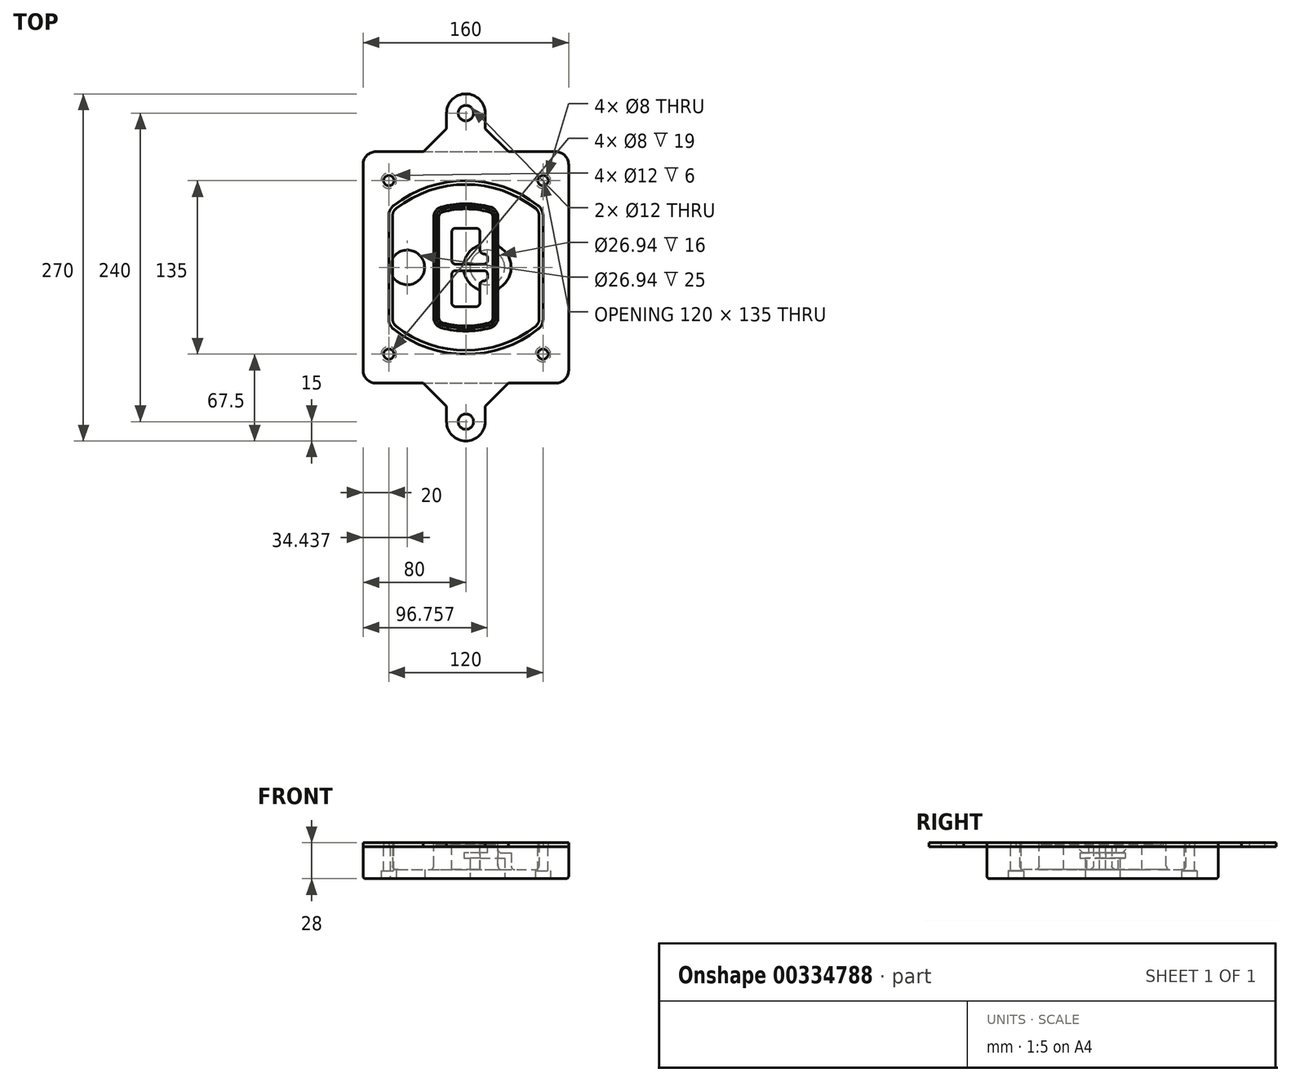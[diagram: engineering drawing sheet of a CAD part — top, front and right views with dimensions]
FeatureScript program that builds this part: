
annotation { "Feature Type Name" : "Feature", "Feature Type Description" : "" }
export const myFeature = defineFeature(function(context is Context, id is Id, definition is map)
    precondition{}
    {
        {
            var Q0;
            Q0=qCreatedBy(makeId("Top.planeOp"),FACE);
            var sketch = newSketch(context, id + "F0", { "sketchPlane" : qUnion([Q0])});
            skPoint(sketch, "E0.rect.middle", {"position": v(0, 0) * mm});
            skLineSegment(sketch, "E1.bottom", {"start": v(-70, -90) * mm, "end": v(70, -90) * mm});
            skLineSegment(sketch, "E1.top", {"start": v(-70, 90) * mm, "end": v(70, 90) * mm});
            skLineSegment(sketch, "E1.left", {"start": v(-80, -80) * mm, "end": v(-80, 80) * mm});
            skLineSegment(sketch, "E1.right", {"start": v(80, -80) * mm, "end": v(80, 80) * mm});
            skLineSegment(sketch, "E2", {"start": v(-80, 90) * mm, "end": v(80, -90) * mm, "construction": true});
            skLineSegment(sketch, "E3", {"start": v(80, 90) * mm, "end": v(-80, -90) * mm, "construction": true});
            skCircle(sketch, "E4", {"center": v(-60, 67.5) * mm, "radius": 4 * mm});
            skCircle(sketch, "E5", {"center": v(60, 67.5) * mm, "radius": 4 * mm});
            skCircle(sketch, "E6", {"center": v(60, -67.5) * mm, "radius": 4 * mm});
            skCircle(sketch, "E7", {"center": v(-60, -67.5) * mm, "radius": 4 * mm});
            skLineSegment(sketch, "E8", {"start": v(-60, 67.5) * mm, "end": v(60, 67.5) * mm, "construction": true});
            skLineSegment(sketch, "E9", {"start": v(60, 67.5) * mm, "end": v(60, -67.5) * mm, "construction": true});
            skLineSegment(sketch, "E10", {"start": v(60, -67.5) * mm, "end": v(-60, -67.5) * mm, "construction": true});
            skLineSegment(sketch, "E11", {"start": v(-60, -67.5) * mm, "end": v(-60, 67.5) * mm, "construction": true});
            skLineSegment(sketch, "E12", {"start": v(-60, 40.3) * mm, "end": v(-60, -40.3) * mm});
            skLineSegment(sketch, "E13", {"start": v(60, 40.3) * mm, "end": v(60, -40.3) * mm});
            skArc(sketch, "E14", {"start": v(56.15, 48.18) * mm, "mid": v(0, 67.5) * mm, "end": v(-56.15, 48.18) * mm});
            skArc(sketch, "E15", {"start": v(-56.15, -48.18) * mm, "mid": v(0, -67.5) * mm, "end": v(56.15, -48.18) * mm});
            skLineSegment(sketch, "E16", {"start": v(-60, 0) * mm, "end": v(60, 0) * mm, "construction": true});
            skPoint(sketch, "E17.visualSharp", {"position": v(-60, -45) * mm});
            skArc(sketch, "E17.filletArc", {"start": v(-60, -40.3) * mm, "mid": v(-58.99, -44.68) * mm, "end": v(-56.15, -48.18) * mm});
            skPoint(sketch, "E18.visualSharp", {"position": v(-60, 45) * mm});
            skArc(sketch, "E18.filletArc", {"start": v(-56.15, 48.18) * mm, "mid": v(-58.99, 44.68) * mm, "end": v(-60, 40.3) * mm});
            skPoint(sketch, "E19.visualSharp", {"position": v(60, 45) * mm});
            skArc(sketch, "E19.filletArc", {"start": v(60, 40.3) * mm, "mid": v(58.99, 44.68) * mm, "end": v(56.15, 48.18) * mm});
            skPoint(sketch, "E20.visualSharp", {"position": v(60, -45) * mm});
            skArc(sketch, "E20.filletArc", {"start": v(56.15, -48.18) * mm, "mid": v(58.99, -44.68) * mm, "end": v(60, -40.3) * mm});
            skPoint(sketch, "E21.visualSharp", {"position": v(-80, 90) * mm});
            skArc(sketch, "E21.filletArc", {"start": v(-70, 90) * mm, "mid": v(-77.07, 87.07) * mm, "end": v(-80, 80) * mm});
            skPoint(sketch, "E22.visualSharp", {"position": v(80, 90) * mm});
            skArc(sketch, "E22.filletArc", {"start": v(80, 80) * mm, "mid": v(77.07, 87.07) * mm, "end": v(70, 90) * mm});
            skPoint(sketch, "E23.visualSharp", {"position": v(80, -90) * mm});
            skArc(sketch, "E23.filletArc", {"start": v(70, -90) * mm, "mid": v(77.07, -87.07) * mm, "end": v(80, -80) * mm});
            skPoint(sketch, "E24.visualSharp", {"position": v(-80, -90) * mm});
            skArc(sketch, "E24.filletArc", {"start": v(-80, -80) * mm, "mid": v(-77.07, -87.07) * mm, "end": v(-70, -90) * mm});
            skArc(sketch, "E25.0", {"start": v(57, 40.3) * mm, "mid": v(56.3, 43.36) * mm, "end": v(54.3, 45.81) * mm});
            skLineSegment(sketch, "E25.1", {"start": v(57, 40.3) * mm, "end": v(57, -40.3) * mm});
            skArc(sketch, "E25.2", {"start": v(54.3, -45.81) * mm, "mid": v(56.3, -43.36) * mm, "end": v(57, -40.3) * mm});
            skArc(sketch, "E25.3", {"start": v(-54.3, -45.81) * mm, "mid": v(0, -64.5) * mm, "end": v(54.3, -45.81) * mm});
            skArc(sketch, "E25.4", {"start": v(-57, -40.3) * mm, "mid": v(-56.3, -43.36) * mm, "end": v(-54.3, -45.81) * mm});
            skArc(sketch, "E25.5", {"start": v(54.3, 45.81) * mm, "mid": v(0, 64.5) * mm, "end": v(-54.3, 45.81) * mm});
            skLineSegment(sketch, "E25.6", {"start": v(-57, 40.3) * mm, "end": v(-57, -40.3) * mm});
            skArc(sketch, "E25.7", {"start": v(-54.3, 45.81) * mm, "mid": v(-56.3, 43.36) * mm, "end": v(-57, 40.3) * mm});
            skArc(sketch, "E26.0", {"start": v(-58.62, 51.33) * mm, "mid": v(-62.58, 46.43) * mm, "end": v(-64, 40.3) * mm});
            skArc(sketch, "E26.1", {"start": v(58.62, 51.33) * mm, "mid": v(0, 71.5) * mm, "end": v(-58.62, 51.33) * mm});
            skArc(sketch, "E26.2", {"start": v(64, 40.3) * mm, "mid": v(62.58, 46.43) * mm, "end": v(58.62, 51.33) * mm});
            skLineSegment(sketch, "E26.3", {"start": v(64, 40.3) * mm, "end": v(64, -40.3) * mm});
            skArc(sketch, "E26.4", {"start": v(58.62, -51.33) * mm, "mid": v(62.58, -46.43) * mm, "end": v(64, -40.3) * mm});
            skLineSegment(sketch, "E26.5", {"start": v(-64, 40.3) * mm, "end": v(-64, -40.3) * mm});
            skArc(sketch, "E26.6", {"start": v(-58.62, -51.33) * mm, "mid": v(0, -71.5) * mm, "end": v(58.62, -51.33) * mm});
            skArc(sketch, "E26.7", {"start": v(-64, -40.3) * mm, "mid": v(-62.58, -46.43) * mm, "end": v(-58.62, -51.33) * mm});
            skSolve(sketch);
        }
        {
            var Q0;
            Q0=makeQuery(id+"F0.imprint","IMPRINT",FACE,{"disambiguationData":[TD([[makeQuery(id+"F0.imprint","IMPRINT",EDGE,{"derivedFrom":sQuery(id+"F0.wireOp",EDGE,"E1.bottom")}),1.0]])]});
            var Q1;
            Q1=makeQuery(id+"F0.imprint","IMPRINT",FACE,{"disambiguationData":[TD([[makeQuery(id+"F0.imprint","IMPRINT",EDGE,{"derivedFrom":sQuery(id+"F0.wireOp",EDGE,"E12")}),1.0]])]});
            var Q2;
            Q2=makeQuery(id+"F0.imprint","IMPRINT",FACE,{"disambiguationData":[TD([[makeQuery(id+"F0.imprint","IMPRINT",EDGE,{"derivedFrom":sQuery(id+"F0.wireOp",EDGE,"E25.0")}),1.0]])]});
            var Q3;
            Q3=makeQuery(id+"F0.imprint","IMPRINT",FACE,{"disambiguationData":[TD([[makeQuery(id+"F0.imprint","IMPRINT",EDGE,{"derivedFrom":sQuery(id+"F0.wireOp",EDGE,"E12")}),-1.0]])]});
            extrude(context, id + "F1", {"entities" : qUnion([Q0, Q1, Q2, Q3]), "oppositeDirection" : true, "depth" : 25 * mm});
        }
        {
            var Q0;
            Q0=makeQuery(id+"F0.imprint","IMPRINT",FACE,{"disambiguationData":[TD([[makeQuery(id+"F0.imprint","IMPRINT",EDGE,{"derivedFrom":sQuery(id+"F0.wireOp",EDGE,"E12")}),1.0]])]});
            extrude(context, id + "F2", {"entities" : qUnion([Q0]), "operationType" : NewBodyOperationType.ADD, "depth" : 3 * mm});
        }
        {
            var Q0;
            Q0=makeQuery(id+"F0.imprint","IMPRINT",FACE,{"disambiguationData":[TD([[makeQuery(id+"F0.imprint","IMPRINT",EDGE,{"derivedFrom":sQuery(id+"F0.wireOp",EDGE,"E25.0")}),1.0]])]});
            extrude(context, id + "F3", {"entities" : qUnion([Q0]), "operationType" : NewBodyOperationType.REMOVE, "oppositeDirection" : true, "depth" : 18 * mm, "offsetDistance" : 25 * mm});
        }
        {
            var Q0;
            Q0=makeQuery(id+"F2.opExtrude","CAP_FACE",FACE,{"disambiguationData":[OSD([sQuery(id+"F0.wireOp",EDGE,"E12"),sQuery(id+"F0.wireOp",EDGE,"E13"),sQuery(id+"F0.wireOp",EDGE,"E14"),sQuery(id+"F0.wireOp",EDGE,"E15"),sQuery(id+"F0.wireOp",EDGE,"E17.filletArc"),sQuery(id+"F0.wireOp",EDGE,"E18.filletArc"),sQuery(id+"F0.wireOp",EDGE,"E19.filletArc"),sQuery(id+"F0.wireOp",EDGE,"E20.filletArc"),sQuery(id+"F0.wireOp",EDGE,"E25.0"),sQuery(id+"F0.wireOp",EDGE,"E25.1"),sQuery(id+"F0.wireOp",EDGE,"E25.2"),sQuery(id+"F0.wireOp",EDGE,"E25.3"),sQuery(id+"F0.wireOp",EDGE,"E25.4"),sQuery(id+"F0.wireOp",EDGE,"E25.5"),sQuery(id+"F0.wireOp",EDGE,"E25.6"),sQuery(id+"F0.wireOp",EDGE,"E25.7")])],"isStart":false});
            var sketch = newSketch(context, id + "F4", { "sketchPlane" : qUnion([Q0])});
            skArc(sketch, "E27.0", {"start": v(-19.08, -46.97) * mm, "mid": v(0, -49.5) * mm, "end": v(19.08, -46.97) * mm});
            skArc(sketch, "E28.0", {"start": v(19.08, 46.97) * mm, "mid": v(0, 49.5) * mm, "end": v(-19.08, 46.97) * mm});
            skLineSegment(sketch, "E29", {"start": v(-25, 39.25) * mm, "end": v(-25, -39.25) * mm});
            skLineSegment(sketch, "E30", {"start": v(25, 39.25) * mm, "end": v(25, -39.25) * mm});
            skLineSegment(sketch, "E31", {"start": v(-25, 45.1) * mm, "end": v(25, 45.1) * mm, "construction": true});
            skLineSegment(sketch, "E32", {"start": v(-25, -45.1) * mm, "end": v(25, -45.1) * mm, "construction": true});
            skPoint(sketch, "E33.visualSharp", {"position": v(-25, 45.1) * mm});
            skArc(sketch, "E33.filletArc", {"start": v(-19.08, 46.97) * mm, "mid": v(-23.35, 44.11) * mm, "end": v(-25, 39.25) * mm});
            skPoint(sketch, "E34.visualSharp", {"position": v(25, 45.1) * mm});
            skArc(sketch, "E34.filletArc", {"start": v(25, 39.25) * mm, "mid": v(23.35, 44.11) * mm, "end": v(19.08, 46.97) * mm});
            skPoint(sketch, "E35.visualSharp", {"position": v(25, -45.1) * mm});
            skArc(sketch, "E35.filletArc", {"start": v(19.08, -46.97) * mm, "mid": v(23.35, -44.11) * mm, "end": v(25, -39.25) * mm});
            skPoint(sketch, "E36.visualSharp", {"position": v(-25, -45.1) * mm});
            skArc(sketch, "E36.filletArc", {"start": v(-25, -39.25) * mm, "mid": v(-23.35, -44.11) * mm, "end": v(-19.08, -46.97) * mm});
            skArc(sketch, "E37.0", {"start": v(54.3, 45.81) * mm, "mid": v(0, 64.5) * mm, "end": v(-54.3, 45.81) * mm});
            skArc(sketch, "E37.1", {"start": v(-54.3, 45.81) * mm, "mid": v(-56.3, 43.36) * mm, "end": v(-57, 40.3) * mm});
            skLineSegment(sketch, "E37.2", {"start": v(-57, 40.3) * mm, "end": v(-57, -40.3) * mm});
            skArc(sketch, "E37.3", {"start": v(-57, -40.3) * mm, "mid": v(-56.3, -43.36) * mm, "end": v(-54.3, -45.81) * mm});
            skArc(sketch, "E37.4", {"start": v(-54.3, -45.81) * mm, "mid": v(0, -64.5) * mm, "end": v(54.3, -45.81) * mm});
            skArc(sketch, "E37.5", {"start": v(54.3, -45.81) * mm, "mid": v(56.3, -43.36) * mm, "end": v(57, -40.3) * mm});
            skLineSegment(sketch, "E37.6", {"start": v(57, 40.3) * mm, "end": v(57, -40.3) * mm});
            skArc(sketch, "E37.7", {"start": v(57, 40.3) * mm, "mid": v(56.3, 43.36) * mm, "end": v(54.3, 45.81) * mm});
            skLineSegment(sketch, "E38.0", {"start": v(23, 39.25) * mm, "end": v(23, -39.25) * mm});
            skArc(sketch, "E38.1", {"start": v(18.56, -45.04) * mm, "mid": v(21.76, -42.9) * mm, "end": v(23, -39.25) * mm});
            skArc(sketch, "E38.2", {"start": v(-18.56, -45.04) * mm, "mid": v(0, -47.5) * mm, "end": v(18.56, -45.04) * mm});
            skArc(sketch, "E38.3", {"start": v(-23, -39.25) * mm, "mid": v(-21.76, -42.9) * mm, "end": v(-18.56, -45.04) * mm});
            skLineSegment(sketch, "E38.4", {"start": v(-23, 39.25) * mm, "end": v(-23, -39.25) * mm});
            skArc(sketch, "E38.5", {"start": v(23, 39.25) * mm, "mid": v(21.76, 42.9) * mm, "end": v(18.56, 45.04) * mm});
            skArc(sketch, "E38.6", {"start": v(-18.56, 45.04) * mm, "mid": v(-21.76, 42.9) * mm, "end": v(-23, 39.25) * mm});
            skArc(sketch, "E38.7", {"start": v(18.56, 45.04) * mm, "mid": v(0, 47.5) * mm, "end": v(-18.56, 45.04) * mm});
            skArc(sketch, "E39.0", {"start": v(21, 39.25) * mm, "mid": v(20.18, 41.68) * mm, "end": v(18.04, 43.1) * mm});
            skLineSegment(sketch, "E39.1", {"start": v(21, 39.25) * mm, "end": v(21, -39.25) * mm});
            skArc(sketch, "E39.2", {"start": v(18.04, -43.1) * mm, "mid": v(20.18, -41.68) * mm, "end": v(21, -39.25) * mm});
            skArc(sketch, "E39.3", {"start": v(-18.04, -43.1) * mm, "mid": v(0, -45.5) * mm, "end": v(18.04, -43.1) * mm});
            skArc(sketch, "E39.4", {"start": v(-21, -39.25) * mm, "mid": v(-20.18, -41.68) * mm, "end": v(-18.04, -43.1) * mm});
            skArc(sketch, "E39.5", {"start": v(18.04, 43.1) * mm, "mid": v(0, 45.5) * mm, "end": v(-18.04, 43.1) * mm});
            skLineSegment(sketch, "E39.6", {"start": v(-21, 39.25) * mm, "end": v(-21, -39.25) * mm});
            skArc(sketch, "E39.7", {"start": v(-18.04, 43.1) * mm, "mid": v(-20.18, 41.68) * mm, "end": v(-21, 39.25) * mm});
            skLineSegment(sketch, "E40", {"start": v(-25, 0) * mm, "end": v(25, 0) * mm, "construction": true});
            skLineSegment(sketch, "E41", {"start": v(-11, 5.5) * mm, "end": v(-11, 27.5) * mm});
            skLineSegment(sketch, "E42", {"start": v(-8, 30.5) * mm, "end": v(8, 30.5) * mm});
            skLineSegment(sketch, "E43", {"start": v(11, 27.5) * mm, "end": v(11, 13.5) * mm});
            skLineSegment(sketch, "E44", {"start": v(14, 10.5) * mm, "end": v(14, 10.5) * mm});
            skLineSegment(sketch, "E45", {"start": v(17, 7.5) * mm, "end": v(17, 5.5) * mm});
            skLineSegment(sketch, "E46", {"start": v(14, 2.5) * mm, "end": v(-8, 2.5) * mm});
            skPoint(sketch, "E47.visualSharp", {"position": v(-11, 30.5) * mm});
            skArc(sketch, "E47.filletArc", {"start": v(-8, 30.5) * mm, "mid": v(-10.12, 29.62) * mm, "end": v(-11, 27.5) * mm});
            skPoint(sketch, "E48.visualSharp", {"position": v(11, 30.5) * mm});
            skArc(sketch, "E48.filletArc", {"start": v(11, 27.5) * mm, "mid": v(10.12, 29.62) * mm, "end": v(8, 30.5) * mm});
            skPoint(sketch, "E49.visualSharp", {"position": v(11, 10.5) * mm});
            skArc(sketch, "E49.filletArc", {"start": v(11, 13.5) * mm, "mid": v(11.88, 11.38) * mm, "end": v(14, 10.5) * mm});
            skPoint(sketch, "E50.visualSharp", {"position": v(17, 10.5) * mm});
            skArc(sketch, "E50.filletArc", {"start": v(17, 7.5) * mm, "mid": v(16.12, 9.62) * mm, "end": v(14, 10.5) * mm});
            skPoint(sketch, "E51.visualSharp", {"position": v(17, 2.5) * mm});
            skArc(sketch, "E51.filletArc", {"start": v(14, 2.5) * mm, "mid": v(16.12, 3.38) * mm, "end": v(17, 5.5) * mm});
            skPoint(sketch, "E52.visualSharp", {"position": v(-11, 2.5) * mm});
            skArc(sketch, "E52.filletArc", {"start": v(-11, 5.5) * mm, "mid": v(-10.12, 3.38) * mm, "end": v(-8, 2.5) * mm});
            skLineSegment(sketch, "E53.0.MirrorCS", {"start": v(14, -2.5) * mm, "end": v(-8, -2.5) * mm});
            skArc(sketch, "E54.0.MirrorCS", {"start": v(-11, -5.5) * mm, "mid": v(-10.12, -3.38) * mm, "end": v(-8, -2.5) * mm});
            skLineSegment(sketch, "E55.0.MirrorCS", {"start": v(-11, -5.5) * mm, "end": v(-11, -27.5) * mm});
            skArc(sketch, "E56.0.MirrorCS", {"start": v(-8, -30.5) * mm, "mid": v(-10.12, -29.62) * mm, "end": v(-11, -27.5) * mm});
            skLineSegment(sketch, "E57.0.MirrorCS", {"start": v(-8, -30.5) * mm, "end": v(8, -30.5) * mm});
            skArc(sketch, "E58.0.MirrorCS", {"start": v(11, -27.5) * mm, "mid": v(10.12, -29.62) * mm, "end": v(8, -30.5) * mm});
            skLineSegment(sketch, "E59.0.MirrorCS", {"start": v(11, -27.5) * mm, "end": v(11, -13.5) * mm});
            skArc(sketch, "E60.0.MirrorCS", {"start": v(11, -13.5) * mm, "mid": v(11.88, -11.38) * mm, "end": v(14, -10.5) * mm});
            skArc(sketch, "E61.0.MirrorCS", {"start": v(17, -7.5) * mm, "mid": v(16.12, -9.62) * mm, "end": v(14, -10.5) * mm});
            skLineSegment(sketch, "E62.0.MirrorCS", {"start": v(17, -7.5) * mm, "end": v(17, -5.5) * mm});
            skArc(sketch, "E63.0.MirrorCS", {"start": v(14, -2.5) * mm, "mid": v(16.12, -3.38) * mm, "end": v(17, -5.5) * mm});
            skSolve(sketch);
        }
        {
            var Q0;
            Q0=makeQuery(id+"F4.imprint","IMPRINT",FACE,{"disambiguationData":[TD([[makeQuery(id+"F4.imprint","IMPRINT",EDGE,{"derivedFrom":sQuery(id+"F4.wireOp",EDGE,"E27.0")}),1.0]])]});
            var Q1;
            Q1=makeQuery(id+"F4.imprint","IMPRINT",FACE,{"disambiguationData":[TD([[makeQuery(id+"F4.imprint","IMPRINT",EDGE,{"derivedFrom":sQuery(id+"F4.wireOp",EDGE,"E38.0")}),-1.0]])]});
            var Q2;
            Q2=makeQuery(id+"F4.imprint","IMPRINT",FACE,{"disambiguationData":[TD([[makeQuery(id+"F4.imprint","IMPRINT",EDGE,{"derivedFrom":sQuery(id+"F4.wireOp",EDGE,"E39.0")}),1.0]])]});
            extrude(context, id + "F5", {"entities" : qUnion([Q0, Q1, Q2]), "operationType" : NewBodyOperationType.ADD, "endBound" : BoundingType.UP_TO_NEXT, "oppositeDirection" : true, "depth" : 25 * mm});
        }
        {
            var Q0;
            Q0=makeQuery(id+"F4.imprint","IMPRINT",FACE,{"disambiguationData":[TD([[makeQuery(id+"F4.imprint","IMPRINT",EDGE,{"derivedFrom":sQuery(id+"F4.wireOp",EDGE,"E38.0")}),-1.0]])]});
            extrude(context, id + "F6", {"entities" : qUnion([Q0]), "operationType" : NewBodyOperationType.REMOVE, "oppositeDirection" : true, "depth" : 2 * mm});
        }
        {
            var Q0;
            Q0=makeQuery(id+"F1.opExtrude","CAP_FACE",FACE,{"disambiguationData":[OSD([sQuery(id+"F0.wireOp",EDGE,"E1.bottom"),sQuery(id+"F0.wireOp",EDGE,"E1.top"),sQuery(id+"F0.wireOp",EDGE,"E1.left"),sQuery(id+"F0.wireOp",EDGE,"E1.right"),sQuery(id+"F0.wireOp",EDGE,"E4"),sQuery(id+"F0.wireOp",EDGE,"E5"),sQuery(id+"F0.wireOp",EDGE,"E6"),sQuery(id+"F0.wireOp",EDGE,"E7"),sQuery(id+"F0.wireOp",EDGE,"E21.filletArc"),sQuery(id+"F0.wireOp",EDGE,"E22.filletArc"),sQuery(id+"F0.wireOp",EDGE,"E23.filletArc"),sQuery(id+"F0.wireOp",EDGE,"E24.filletArc")])],"isStart":false});
            var sketch = newSketch(context, id + "F7", { "sketchPlane" : qUnion([Q0])});
            skCircle(sketch, "E64", {"center": v(16.76, 0) * mm, "radius": 13.47 * mm});
            skCircle(sketch, "E65", {"center": v(-45.56, 0) * mm, "radius": 13.47 * mm});
            skLineSegment(sketch, "E66", {"start": v(80, 0) * mm, "end": v(-80, 0) * mm});
            skCircle(sketch, "E67", {"center": v(16.76, 0) * mm, "radius": 18.47 * mm});
            skCircle(sketch, "E68", {"center": v(60, -67.5) * mm, "radius": 6 * mm});
            skCircle(sketch, "E69", {"center": v(-60, -67.5) * mm, "radius": 6 * mm});
            skCircle(sketch, "E70", {"center": v(-60, 67.5) * mm, "radius": 6 * mm});
            skCircle(sketch, "E71", {"center": v(60, 67.5) * mm, "radius": 6 * mm});
            skSolve(sketch);
        }
        {
            var Q0;
            {var subQ1=sQuery(id+"F7.wireOp",EDGE,"E66");var subQ4=sQuery(id+"F7.wireOp",EDGE,"E64");var subQ6=makeQuery(id+"F7.imprint","INTERSECT",VERTEX,{"disambiguationData":[OD(0.0)],"derivedFrom":[subQ4,subQ1]});Q0=makeQuery(id+"F7.imprint","IMPRINT",FACE,{"disambiguationData":[TD([[makeQuery(id+"F7.imprint","IMPRINT",EDGE,{"disambiguationData":[TD([[subQ6,-1.0]])],"derivedFrom":subQ4}),-1.0]])]});}
            var Q1;
            {var subQ0=sQuery(id+"F7.wireOp",EDGE,"E66");var subQ1=sQuery(id+"F7.wireOp",EDGE,"E64");var subQ3=makeQuery(id+"F7.imprint","INTERSECT",VERTEX,{"disambiguationData":[OD(0.0)],"derivedFrom":[subQ1,subQ0]});Q1=makeQuery(id+"F7.imprint","IMPRINT",FACE,{"disambiguationData":[TD([[makeQuery(id+"F7.imprint","IMPRINT",EDGE,{"disambiguationData":[TD([[subQ3,-1.0]])],"derivedFrom":subQ1}),1.0]])]});}
            var Q2;
            {var subQ0=sQuery(id+"F7.wireOp",EDGE,"E66");var subQ1=sQuery(id+"F7.wireOp",EDGE,"E64");var subQ3=makeQuery(id+"F7.imprint","INTERSECT",VERTEX,{"disambiguationData":[OD(0.0)],"derivedFrom":[subQ1,subQ0]});Q2=makeQuery(id+"F7.imprint","IMPRINT",FACE,{"disambiguationData":[TD([[makeQuery(id+"F7.imprint","IMPRINT",EDGE,{"disambiguationData":[TD([[subQ3,1.0]])],"derivedFrom":subQ1}),1.0]])]});}
            var Q3;
            {var subQ1=sQuery(id+"F7.wireOp",EDGE,"E66");var subQ4=sQuery(id+"F7.wireOp",EDGE,"E64");var subQ6=makeQuery(id+"F7.imprint","INTERSECT",VERTEX,{"disambiguationData":[OD(0.0)],"derivedFrom":[subQ4,subQ1]});Q3=makeQuery(id+"F7.imprint","IMPRINT",FACE,{"disambiguationData":[TD([[makeQuery(id+"F7.imprint","IMPRINT",EDGE,{"disambiguationData":[TD([[subQ6,1.0]])],"derivedFrom":subQ4}),-1.0]])]});}
            extrude(context, id + "F8", {"entities" : qUnion([Q0, Q1, Q2, Q3]), "operationType" : NewBodyOperationType.ADD, "oppositeDirection" : true, "depth" : 20 * mm});
        }
        {
            var Q0;
            {var subQ0=sQuery(id+"F7.wireOp",EDGE,"E66");var subQ1=sQuery(id+"F7.wireOp",EDGE,"E64");var subQ3=makeQuery(id+"F7.imprint","INTERSECT",VERTEX,{"disambiguationData":[OD(0.0)],"derivedFrom":[subQ1,subQ0]});Q0=makeQuery(id+"F7.imprint","IMPRINT",FACE,{"disambiguationData":[TD([[makeQuery(id+"F7.imprint","IMPRINT",EDGE,{"disambiguationData":[TD([[subQ3,-1.0]])],"derivedFrom":subQ1}),1.0]])]});}
            var Q1;
            {var subQ0=sQuery(id+"F7.wireOp",EDGE,"E66");var subQ1=sQuery(id+"F7.wireOp",EDGE,"E64");var subQ3=makeQuery(id+"F7.imprint","INTERSECT",VERTEX,{"disambiguationData":[OD(0.0)],"derivedFrom":[subQ1,subQ0]});Q1=makeQuery(id+"F7.imprint","IMPRINT",FACE,{"disambiguationData":[TD([[makeQuery(id+"F7.imprint","IMPRINT",EDGE,{"disambiguationData":[TD([[subQ3,1.0]])],"derivedFrom":subQ1}),1.0]])]});}
            extrude(context, id + "F9", {"entities" : qUnion([Q0, Q1]), "operationType" : NewBodyOperationType.REMOVE, "oppositeDirection" : true, "depth" : 16 * mm});
        }
        {
            var Q0;
            {var subQ0=sQuery(id+"F7.wireOp",EDGE,"E66");var subQ1=sQuery(id+"F7.wireOp",EDGE,"E65");var subQ3=makeQuery(id+"F7.imprint","INTERSECT",VERTEX,{"disambiguationData":[OD(0.0)],"derivedFrom":[subQ1,subQ0]});Q0=makeQuery(id+"F7.imprint","IMPRINT",FACE,{"disambiguationData":[TD([[makeQuery(id+"F7.imprint","IMPRINT",EDGE,{"disambiguationData":[TD([[subQ3,-1.0]])],"derivedFrom":subQ1}),1.0]])]});}
            var Q1;
            {var subQ0=sQuery(id+"F7.wireOp",EDGE,"E66");var subQ1=sQuery(id+"F7.wireOp",EDGE,"E65");var subQ3=makeQuery(id+"F7.imprint","INTERSECT",VERTEX,{"disambiguationData":[OD(0.0)],"derivedFrom":[subQ1,subQ0]});Q1=makeQuery(id+"F7.imprint","IMPRINT",FACE,{"disambiguationData":[TD([[makeQuery(id+"F7.imprint","IMPRINT",EDGE,{"disambiguationData":[TD([[subQ3,1.0]])],"derivedFrom":subQ1}),1.0]])]});}
            extrude(context, id + "F10", {"entities" : qUnion([Q0, Q1]), "operationType" : NewBodyOperationType.REMOVE, "oppositeDirection" : true, "depth" : 25 * mm});
        }
        {
            var Q0;
            Q0=makeQuery(id+"F7.imprint","IMPRINT",FACE,{"disambiguationData":[TD([[makeQuery(id+"F7.imprint","IMPRINT",EDGE,{"derivedFrom":sQuery(id+"F7.wireOp",EDGE,"E68")}),1.0]])]});
            var Q1;
            Q1=makeQuery(id+"F7.imprint","IMPRINT",FACE,{"disambiguationData":[TD([[makeQuery(id+"F7.imprint","IMPRINT",EDGE,{"derivedFrom":makeQuery(id+"F1.opExtrude","CAP_EDGE",EDGE,{"disambiguationData":[OSD([sQuery(id+"F0.wireOp",EDGE,"E5")])],"isStart":false})}),-1.0]])]});
            var Q2;
            Q2=makeQuery(id+"F7.imprint","IMPRINT",FACE,{"disambiguationData":[TD([[makeQuery(id+"F7.imprint","IMPRINT",EDGE,{"derivedFrom":sQuery(id+"F7.wireOp",EDGE,"E69")}),1.0]])]});
            var Q3;
            Q3=makeQuery(id+"F7.imprint","IMPRINT",FACE,{"disambiguationData":[TD([[makeQuery(id+"F7.imprint","IMPRINT",EDGE,{"derivedFrom":makeQuery(id+"F1.opExtrude","CAP_EDGE",EDGE,{"disambiguationData":[OSD([sQuery(id+"F0.wireOp",EDGE,"E4")])],"isStart":false})}),-1.0]])]});
            var Q4;
            Q4=makeQuery(id+"F7.imprint","IMPRINT",FACE,{"disambiguationData":[TD([[makeQuery(id+"F7.imprint","IMPRINT",EDGE,{"derivedFrom":sQuery(id+"F7.wireOp",EDGE,"E70")}),1.0]])]});
            var Q5;
            Q5=makeQuery(id+"F7.imprint","IMPRINT",FACE,{"disambiguationData":[TD([[makeQuery(id+"F7.imprint","IMPRINT",EDGE,{"derivedFrom":makeQuery(id+"F1.opExtrude","CAP_EDGE",EDGE,{"disambiguationData":[OSD([sQuery(id+"F0.wireOp",EDGE,"E7")])],"isStart":false})}),-1.0]])]});
            var Q6;
            Q6=makeQuery(id+"F7.imprint","IMPRINT",FACE,{"disambiguationData":[TD([[makeQuery(id+"F7.imprint","IMPRINT",EDGE,{"derivedFrom":sQuery(id+"F7.wireOp",EDGE,"E71")}),1.0]])]});
            var Q7;
            Q7=makeQuery(id+"F7.imprint","IMPRINT",FACE,{"disambiguationData":[TD([[makeQuery(id+"F7.imprint","IMPRINT",EDGE,{"derivedFrom":makeQuery(id+"F1.opExtrude","CAP_EDGE",EDGE,{"disambiguationData":[OSD([sQuery(id+"F0.wireOp",EDGE,"E6")])],"isStart":false})}),-1.0]])]});
            extrude(context, id + "F11", {"entities" : qUnion([Q0, Q1, Q2, Q3, Q4, Q5, Q6, Q7]), "operationType" : NewBodyOperationType.REMOVE, "oppositeDirection" : true, "depth" : 6 * mm});
        }
        {
            var Q0;
            Q0=makeQuery(id+"F9.boolean.opBoolean","COPY",FACE,{"derivedFrom":makeQuery(id+"F9.opExtrude","CAP_FACE",FACE,{"disambiguationData":[OSD([sQuery(id+"F7.wireOp",EDGE,"E64")])],"isStart":false})});
            var sketch = newSketch(context, id + "F12", { "sketchPlane" : qUnion([Q0])});
            skArc(sketch, "E72.0", {"start": v(11, 17.55) * mm, "mid": v(2.57, 11.82) * mm, "end": v(-1.54, 2.5) * mm});
            skArc(sketch, "E72.1", {"start": v(-1.54, -2.5) * mm, "mid": v(2.57, -11.82) * mm, "end": v(11, -17.55) * mm});
            skLineSegment(sketch, "E73", {"start": v(-1.54, -2.5) * mm, "end": v(14, -2.5) * mm});
            skLineSegment(sketch, "E74.0", {"start": v(14, 2.5) * mm, "end": v(-1.54, 2.5) * mm});
            skArc(sketch, "E74.1", {"start": v(14, 2.5) * mm, "mid": v(16.12, 3.38) * mm, "end": v(17, 5.5) * mm});
            skLineSegment(sketch, "E74.2", {"start": v(17, 7.5) * mm, "end": v(17, 5.5) * mm});
            skArc(sketch, "E74.3", {"start": v(17, 7.5) * mm, "mid": v(16.12, 9.62) * mm, "end": v(14, 10.5) * mm});
            skArc(sketch, "E74.4", {"start": v(11, 13.5) * mm, "mid": v(11.88, 11.38) * mm, "end": v(14, 10.5) * mm});
            skLineSegment(sketch, "E74.5", {"start": v(11, 17.55) * mm, "end": v(11, 13.5) * mm});
            skLineSegment(sketch, "E74.7", {"start": v(14, -2.5) * mm, "end": v(-1.54, -2.5) * mm});
            skArc(sketch, "E74.8", {"start": v(14, -2.5) * mm, "mid": v(16.12, -3.38) * mm, "end": v(17, -5.5) * mm});
            skLineSegment(sketch, "E74.9", {"start": v(17, -7.5) * mm, "end": v(17, -5.5) * mm});
            skArc(sketch, "E74.10", {"start": v(17, -7.5) * mm, "mid": v(16.12, -9.62) * mm, "end": v(14, -10.5) * mm});
            skArc(sketch, "E74.11", {"start": v(11, -13.5) * mm, "mid": v(11.88, -11.38) * mm, "end": v(14, -10.5) * mm});
            skLineSegment(sketch, "E74.12", {"start": v(11, -17.55) * mm, "end": v(11, -13.5) * mm});
            skPoint(sketch, "E75.orphan", {"position": v(11, -27.5) * mm});
            skPoint(sketch, "E76.orphan", {"position": v(-8, -2.5) * mm});
            skPoint(sketch, "E77.orphan", {"position": v(-8, 2.5) * mm});
            skPoint(sketch, "E78.orphan", {"position": v(11, 27.5) * mm});
            skSolve(sketch);
        }
        {
            var Q0;
            {var subQ7=sQuery(id+"F12.wireOp",EDGE,"E72.0");var subQ14=sQuery(id+"F12.wireOp",EDGE,"E72.1");var subQ16=sQuery(id+"F12.wireOp",EDGE,"E74.1");var subQ18=sQuery(id+"F12.wireOp",EDGE,"E74.8");Q0=qUnion([makeQuery(id+"F12.imprint","IMPRINT",FACE,{"disambiguationData":[TD([[makeQuery(id+"F12.imprint","IMPRINT",EDGE,{"derivedFrom":subQ7}),1.0]])]}),makeQuery(id+"F12.imprint","IMPRINT",FACE,{"disambiguationData":[TD([[makeQuery(id+"F12.imprint","IMPRINT",EDGE,{"derivedFrom":subQ14}),1.0]])]}),makeQuery(id+"F12.imprint","IMPRINT",FACE,{"disambiguationData":[TD([[makeQuery(id+"F12.imprint","IMPRINT",EDGE,{"derivedFrom":subQ16}),1.0]])]}),makeQuery(id+"F12.imprint","IMPRINT",FACE,{"disambiguationData":[TD([[makeQuery(id+"F12.imprint","IMPRINT",EDGE,{"derivedFrom":subQ18}),-1.0]])]})]);}
            var Q1;
            Q1=makeQuery(id+"F5.boolean.opBoolean","SPLIT",FACE,{"disambiguationData":[TD([makeQuery(id+"F5.opExtrude","SWEPT_FACE",FACE,{"disambiguationData":[OSD([sQuery(id+"F4.wireOp",EDGE,"E41")])]})])],"derivedFrom":makeQuery(id+"F3.boolean.opBoolean","COPY",FACE,{"derivedFrom":makeQuery(id+"F3.opExtrude","CAP_FACE",FACE,{"disambiguationData":[OSD([sQuery(id+"F0.wireOp",EDGE,"E25.0"),sQuery(id+"F0.wireOp",EDGE,"E25.1"),sQuery(id+"F0.wireOp",EDGE,"E25.2"),sQuery(id+"F0.wireOp",EDGE,"E25.3"),sQuery(id+"F0.wireOp",EDGE,"E25.4"),sQuery(id+"F0.wireOp",EDGE,"E25.5"),sQuery(id+"F0.wireOp",EDGE,"E25.6"),sQuery(id+"F0.wireOp",EDGE,"E25.7")])],"isStart":false})})});
            extrude(context, id + "F13", {"entities" : qUnion([Q0]), "operationType" : NewBodyOperationType.REMOVE, "endBound" : BoundingType.UP_TO_SURFACE, "endBoundEntityFace" : qUnion([Q1]), "depth" : 25 * mm});
        }
        {
            var Q0;
            Q0=makeQuery(id+"F3.boolean.opBoolean","COPY",EDGE,{"derivedFrom":makeQuery(id+"F3.opExtrude","CAP_EDGE",EDGE,{"disambiguationData":[OSD([sQuery(id+"F0.wireOp",EDGE,"E25.6")])],"isStart":false})});
            var Q1;
            Q1=makeQuery(id+"F8.boolean.opBoolean","INTERSECT",EDGE,{"derivedFrom":[makeQuery(id+"F5.opExtrude","SWEPT_FACE",FACE,{"disambiguationData":[OSD([sQuery(id+"F4.wireOp",EDGE,"E30")])]}),makeQuery(id+"F8.opExtrude","CAP_FACE",FACE,{"disambiguationData":[OSD([sQuery(id+"F7.wireOp",EDGE,"E67")])],"isStart":false})]});
            var Q2;
            Q2=makeQuery(id+"F8.boolean.opBoolean","INTERSECT",EDGE,{"disambiguationData":[OD(1.0)],"derivedFrom":[makeQuery(id+"F5.opExtrude","SWEPT_FACE",FACE,{"disambiguationData":[OSD([sQuery(id+"F4.wireOp",EDGE,"E30")])]}),makeQuery(id+"F8.opExtrude","SWEPT_FACE",FACE,{"disambiguationData":[OSD([sQuery(id+"F7.wireOp",EDGE,"E67")])]})]});
            var Q3;
            {var subQ0=sQuery(id+"F4.wireOp",EDGE,"E30");Q3=makeQuery(id+"F8.boolean.opBoolean","SPLIT",EDGE,{"disambiguationData":[TD([makeQuery(id+"F5.opExtrude","SWEPT_FACE",FACE,{"disambiguationData":[OSD([sQuery(id+"F4.wireOp",EDGE,"E35.filletArc")])]})])],"derivedFrom":makeQuery(id+"F5.opExtrude","CAP_EDGE",EDGE,{"disambiguationData":[OSD([subQ0])],"isStart":false})});}
            var Q4;
            {var subQ0=sQuery(id+"F0.wireOp",EDGE,"E25.7");var subQ1=sQuery(id+"F0.wireOp",EDGE,"E25.1");var subQ2=sQuery(id+"F0.wireOp",EDGE,"E25.6");var subQ3=sQuery(id+"F0.wireOp",EDGE,"E25.5");var subQ4=sQuery(id+"F0.wireOp",EDGE,"E25.4");var subQ5=sQuery(id+"F0.wireOp",EDGE,"E25.0");var subQ6=sQuery(id+"F0.wireOp",EDGE,"E25.2");var subQ7=sQuery(id+"F0.wireOp",EDGE,"E25.3");Q4=makeQuery(id+"F8.boolean.opBoolean","INTERSECT",EDGE,{"derivedFrom":[makeQuery(id+"F5.boolean.opBoolean","SPLIT",FACE,{"disambiguationData":[TD([makeQuery(id+"F2.opExtrude","SWEPT_FACE",FACE,{"disambiguationData":[OSD([subQ5])]})])],"derivedFrom":makeQuery(id+"F3.boolean.opBoolean","COPY",FACE,{"derivedFrom":makeQuery(id+"F3.opExtrude","CAP_FACE",FACE,{"disambiguationData":[OSD([subQ5,subQ1,subQ6,subQ7,subQ4,subQ3,subQ2,subQ0])],"isStart":false})})}),makeQuery(id+"F8.opExtrude","SWEPT_FACE",FACE,{"disambiguationData":[OSD([sQuery(id+"F7.wireOp",EDGE,"E67")])]})]});}
            var Q5;
            Q5=makeQuery(id+"F8.boolean.opBoolean","INTERSECT",EDGE,{"disambiguationData":[OD(0.0)],"derivedFrom":[makeQuery(id+"F5.opExtrude","SWEPT_FACE",FACE,{"disambiguationData":[OSD([sQuery(id+"F4.wireOp",EDGE,"E30")])]}),makeQuery(id+"F8.opExtrude","SWEPT_FACE",FACE,{"disambiguationData":[OSD([sQuery(id+"F7.wireOp",EDGE,"E67")])]})]});
            fillet(context, id + "F14", {"entities" : qUnion([Q0, Q1, Q2, Q3, Q4, Q5]), "radius" : 3 * mm, "tangentPropagation" : true, "allowEdgeOverflow" : false});
        }
        {
            var Q0;
            Q0=makeQuery(id+"F1.opExtrude","CAP_EDGE",EDGE,{"disambiguationData":[OSD([sQuery(id+"F0.wireOp",EDGE,"E1.bottom")])],"isStart":false});
            fillet(context, id + "F15", {"entities" : qUnion([Q0]), "radius" : 2 * mm, "tangentPropagation" : true, "allowEdgeOverflow" : false});
        }
        {
            var Q0;
            {var subQ0=sQuery(id+"F0.wireOp",EDGE,"E21.filletArc");var subQ1=sQuery(id+"F0.wireOp",EDGE,"E7");var subQ2=sQuery(id+"F0.wireOp",EDGE,"E6");var subQ3=sQuery(id+"F0.wireOp",EDGE,"E5");var subQ4=sQuery(id+"F0.wireOp",EDGE,"E4");var subQ5=sQuery(id+"F0.wireOp",EDGE,"E22.filletArc");var subQ6=sQuery(id+"F0.wireOp",EDGE,"E1.bottom");var subQ7=sQuery(id+"F0.wireOp",EDGE,"E1.right");var subQ8=sQuery(id+"F0.wireOp",EDGE,"E1.top");var subQ9=sQuery(id+"F0.wireOp",EDGE,"E1.left");var subQ10=sQuery(id+"F0.wireOp",EDGE,"E23.filletArc");var subQ11=sQuery(id+"F0.wireOp",EDGE,"E24.filletArc");Q0=makeQuery(id+"F2.boolean.opBoolean","SPLIT",FACE,{"disambiguationData":[TD([makeQuery(id+"F1.opExtrude","SWEPT_FACE",FACE,{"disambiguationData":[OSD([subQ6])]})])],"derivedFrom":makeQuery(id+"F1.opExtrude","CAP_FACE",FACE,{"disambiguationData":[OSD([subQ6,subQ8,subQ9,subQ7,subQ4,subQ3,subQ2,subQ1,subQ0,subQ5,subQ10,subQ11])],"isStart":true})});}
            var sketch = newSketch(context, id + "F16", { "sketchPlane" : qUnion([Q0])});
            skLineSegment(sketch, "E79", {"start": v(0, 90) * mm, "end": v(0, 120) * mm, "construction": true});
            skCircle(sketch, "E80", {"center": v(0, 120) * mm, "radius": 6 * mm});
            skLineSegment(sketch, "E81", {"start": v(-33, 90) * mm, "end": v(-15, 108) * mm});
            skLineSegment(sketch, "E82", {"start": v(-15, 108) * mm, "end": v(-15, 120) * mm});
            skLineSegment(sketch, "E83", {"start": v(33.1, 90) * mm, "end": v(15, 108) * mm});
            skLineSegment(sketch, "E84", {"start": v(15, 108) * mm, "end": v(15, 120) * mm});
            skArc(sketch, "E85", {"start": v(15, 120) * mm, "mid": v(0, 135) * mm, "end": v(-15, 120) * mm});
            skArc(sketch, "E86.MirrorCS", {"start": v(-15, 120) * mm, "mid": v(0, 135) * mm, "end": v(15, 120) * mm});
            skLineSegment(sketch, "E87.MirrorCS", {"start": v(-33.1, 90) * mm, "end": v(-15, 108) * mm});
            skLineSegment(sketch, "E88.MirrorCS", {"start": v(33, 90) * mm, "end": v(15, 108) * mm});
            skLineSegment(sketch, "E89", {"start": v(-80, 0) * mm, "end": v(80, 0) * mm, "construction": true});
            skLineSegment(sketch, "E90.MirrorCS", {"start": v(-33.1, -90) * mm, "end": v(-15, -108) * mm});
            skArc(sketch, "E91.MirrorCS", {"start": v(-15, -120) * mm, "mid": v(0, -135) * mm, "end": v(15, -120) * mm});
            skLineSegment(sketch, "E92.MirrorCS", {"start": v(15, -108) * mm, "end": v(15, -120) * mm});
            skLineSegment(sketch, "E93.MirrorCS", {"start": v(33, -90) * mm, "end": v(15, -108) * mm});
            skCircle(sketch, "E94.MirrorC", {"center": v(0, -120) * mm, "radius": 6 * mm});
            skLineSegment(sketch, "E95.MirrorCS", {"start": v(0, -90) * mm, "end": v(0, -120) * mm, "construction": true});
            skLineSegment(sketch, "E96.MirrorCS", {"start": v(-15, -108) * mm, "end": v(-15, -120) * mm});
            skSolve(sketch);
        }
        {
            var Q0;
            {var subQ0=sQuery(id+"F16.wireOp",EDGE,"E81");Q0=makeQuery(id+"F16.imprint","IMPRINT",FACE,{"disambiguationData":[TD([[makeQuery(id+"F16.imprint","IMPRINT",EDGE,{"derivedFrom":subQ0}),-1.0]])]});}
            var Q1;
            Q1=makeQuery(id+"F16.imprint","IMPRINT",FACE,{"disambiguationData":[TD([[makeQuery(id+"F16.imprint","IMPRINT",EDGE,{"derivedFrom":makeQuery(id+"F1.opExtrude","CAP_EDGE",EDGE,{"disambiguationData":[OSD([sQuery(id+"F0.wireOp",EDGE,"E1.left")])],"isStart":true})}),-1.0]])]});
            var Q2;
            {var subQ1=sQuery(id+"F16.wireOp",EDGE,"E90.MirrorCS");Q2=makeQuery(id+"F16.imprint","IMPRINT",FACE,{"disambiguationData":[TD([[makeQuery(id+"F16.imprint","IMPRINT",EDGE,{"derivedFrom":subQ1}),1.0]])]});}
            var Q3;
            Q3=makeQuery(id+"F2.opExtrude","CAP_FACE",FACE,{"disambiguationData":[OSD([sQuery(id+"F0.wireOp",EDGE,"E12"),sQuery(id+"F0.wireOp",EDGE,"E13"),sQuery(id+"F0.wireOp",EDGE,"E14"),sQuery(id+"F0.wireOp",EDGE,"E15"),sQuery(id+"F0.wireOp",EDGE,"E17.filletArc"),sQuery(id+"F0.wireOp",EDGE,"E18.filletArc"),sQuery(id+"F0.wireOp",EDGE,"E19.filletArc"),sQuery(id+"F0.wireOp",EDGE,"E20.filletArc"),sQuery(id+"F0.wireOp",EDGE,"E25.0"),sQuery(id+"F0.wireOp",EDGE,"E25.1"),sQuery(id+"F0.wireOp",EDGE,"E25.2"),sQuery(id+"F0.wireOp",EDGE,"E25.3"),sQuery(id+"F0.wireOp",EDGE,"E25.4"),sQuery(id+"F0.wireOp",EDGE,"E25.5"),sQuery(id+"F0.wireOp",EDGE,"E25.6"),sQuery(id+"F0.wireOp",EDGE,"E25.7")])],"isStart":false});
            extrude(context, id + "F17", {"entities" : qUnion([Q0, Q1, Q2]), "endBound" : BoundingType.UP_TO_SURFACE, "endBoundEntityFace" : qUnion([Q3]), "depth" : 25 * mm});
        }
    });
